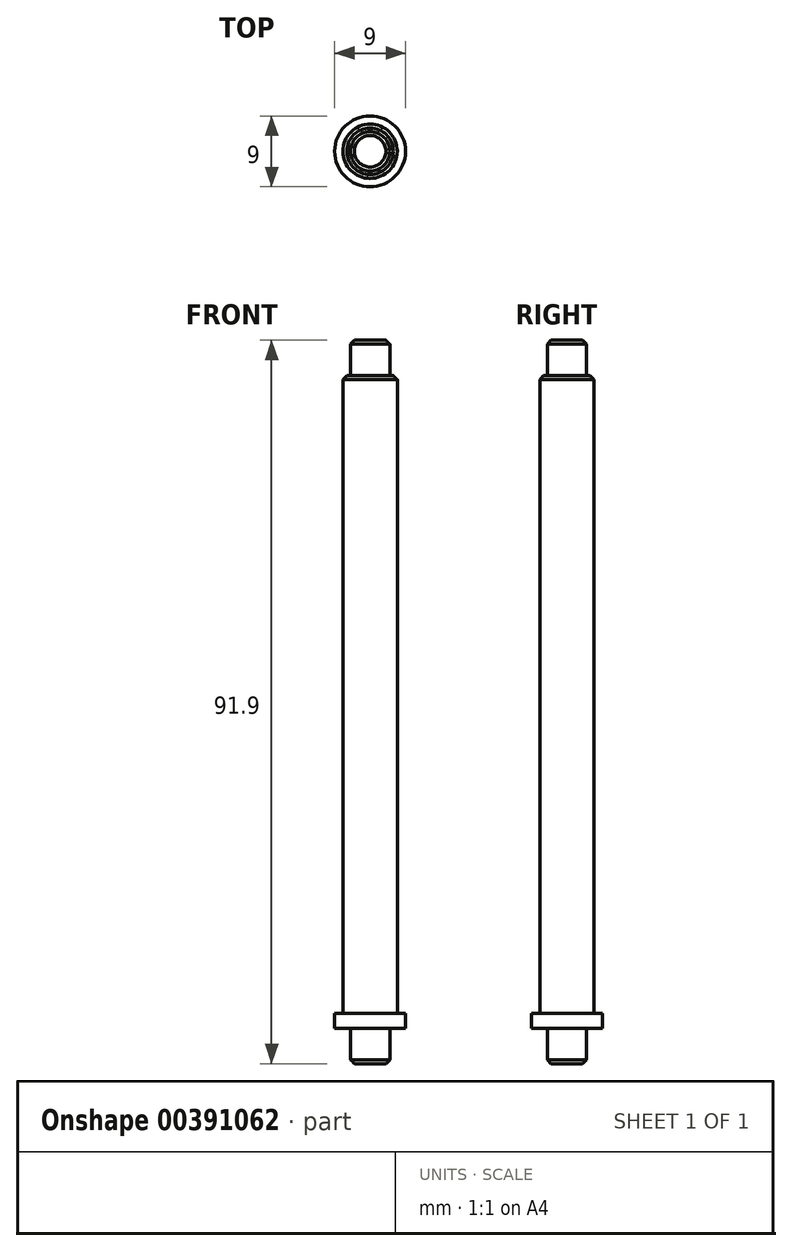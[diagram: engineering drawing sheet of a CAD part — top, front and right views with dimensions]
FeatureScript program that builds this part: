
annotation { "Feature Type Name" : "Feature", "Feature Type Description" : "" }
export const myFeature = defineFeature(function(context is Context, id is Id, definition is map)
    precondition{}
    {
        {
            var Q0;
            Q0=qCreatedBy(makeId("Top.planeOp"),FACE);
            var sketch = newSketch(context, id + "F0", { "sketchPlane" : qUnion([Q0])});
            skCircle(sketch, "E0", {"center": v(0, 0) * mm, "radius": 3.45 * mm});
            skCircle(sketch, "E1", {"center": v(0, 0) * mm, "radius": 4.5 * mm});
            skSolve(sketch);
        }
        {
            var Q0;
            Q0=makeQuery(id+"F0.imprint","IMPRINT",FACE,{"disambiguationData":[TD([[makeQuery(id+"F0.imprint","IMPRINT",EDGE,{"derivedFrom":sQuery(id+"F0.wireOp",EDGE,"E0")}),1.0]])]});
            extrude(context, id + "F1", {"entities" : qUnion([Q0]), "depth" : 81 * mm});
        }
        {
            var Q0;
            Q0=makeQuery(id+"F1.opExtrude","CAP_FACE",FACE,{"disambiguationData":[OSD([sQuery(id+"F0.wireOp",EDGE,"E0")])],"isStart":false});
            var sketch = newSketch(context, id + "F2", { "sketchPlane" : qUnion([Q0])});
            skPoint(sketch, "E2.0", {"position": v(0, 0) * mm});
            skCircle(sketch, "E3", {"center": v(0, 0) * mm, "radius": 2.5 * mm});
            skSolve(sketch);
        }
        {
            var Q0;
            Q0=makeQuery(id+"F2.imprint","IMPRINT",FACE,{"disambiguationData":[TD([[makeQuery(id+"F2.imprint","IMPRINT",EDGE,{"derivedFrom":sQuery(id+"F2.wireOp",EDGE,"E3")}),1.0]])]});
            extrude(context, id + "F3", {"entities" : qUnion([Q0]), "operationType" : NewBodyOperationType.ADD, "depth" : 4.5 * mm});
        }
        {
            var Q0;
            Q0=makeQuery(id+"F0.imprint","IMPRINT",FACE,{"disambiguationData":[TD([[makeQuery(id+"F0.imprint","IMPRINT",EDGE,{"derivedFrom":sQuery(id+"F0.wireOp",EDGE,"E0")}),1.0]])]});
            var Q1;
            Q1=makeQuery(id+"F0.imprint","IMPRINT",FACE,{"disambiguationData":[TD([[makeQuery(id+"F0.imprint","IMPRINT",EDGE,{"derivedFrom":sQuery(id+"F0.wireOp",EDGE,"E0")}),-1.0]])]});
            extrude(context, id + "F4", {"entities" : qUnion([Q0, Q1]), "operationType" : NewBodyOperationType.ADD, "oppositeDirection" : true, "depth" : 1.9 * mm});
        }
        {
            var Q0;
            Q0=makeQuery(id+"F4.opExtrude","CAP_FACE",FACE,{"disambiguationData":[OSD([sQuery(id+"F0.wireOp",EDGE,"E1")])],"isStart":false});
            var sketch = newSketch(context, id + "F5", { "sketchPlane" : qUnion([Q0])});
            skCircle(sketch, "E4", {"center": v(0, 0) * mm, "radius": 2.5 * mm});
            skSolve(sketch);
        }
        {
            var Q0;
            Q0=makeQuery(id+"F5.imprint","IMPRINT",FACE,{"disambiguationData":[TD([[makeQuery(id+"F5.imprint","IMPRINT",EDGE,{"derivedFrom":sQuery(id+"F5.wireOp",EDGE,"E4")}),1.0]])]});
            extrude(context, id + "F6", {"entities" : qUnion([Q0]), "operationType" : NewBodyOperationType.ADD, "depth" : 4.5 * mm});
        }
        {
            var Q0;
            Q0=makeQuery(id+"F3.opExtrude","CAP_EDGE",EDGE,{"disambiguationData":[OSD([sQuery(id+"F2.wireOp",EDGE,"E3")])],"isStart":false});
            var Q1;
            Q1=makeQuery(id+"F1.opExtrude","CAP_EDGE",EDGE,{"disambiguationData":[OSD([sQuery(id+"F0.wireOp",EDGE,"E0")])],"isStart":false});
            var Q2;
            Q2=makeQuery(id+"F6.opExtrude","CAP_EDGE",EDGE,{"disambiguationData":[OSD([sQuery(id+"F5.wireOp",EDGE,"E4")])],"isStart":false});
            chamfer(context, id + "F7", {"entities" : qUnion([Q0, Q1, Q2]), "width" : .5 * mm, "tangentPropagation" : true});
        }
    });
